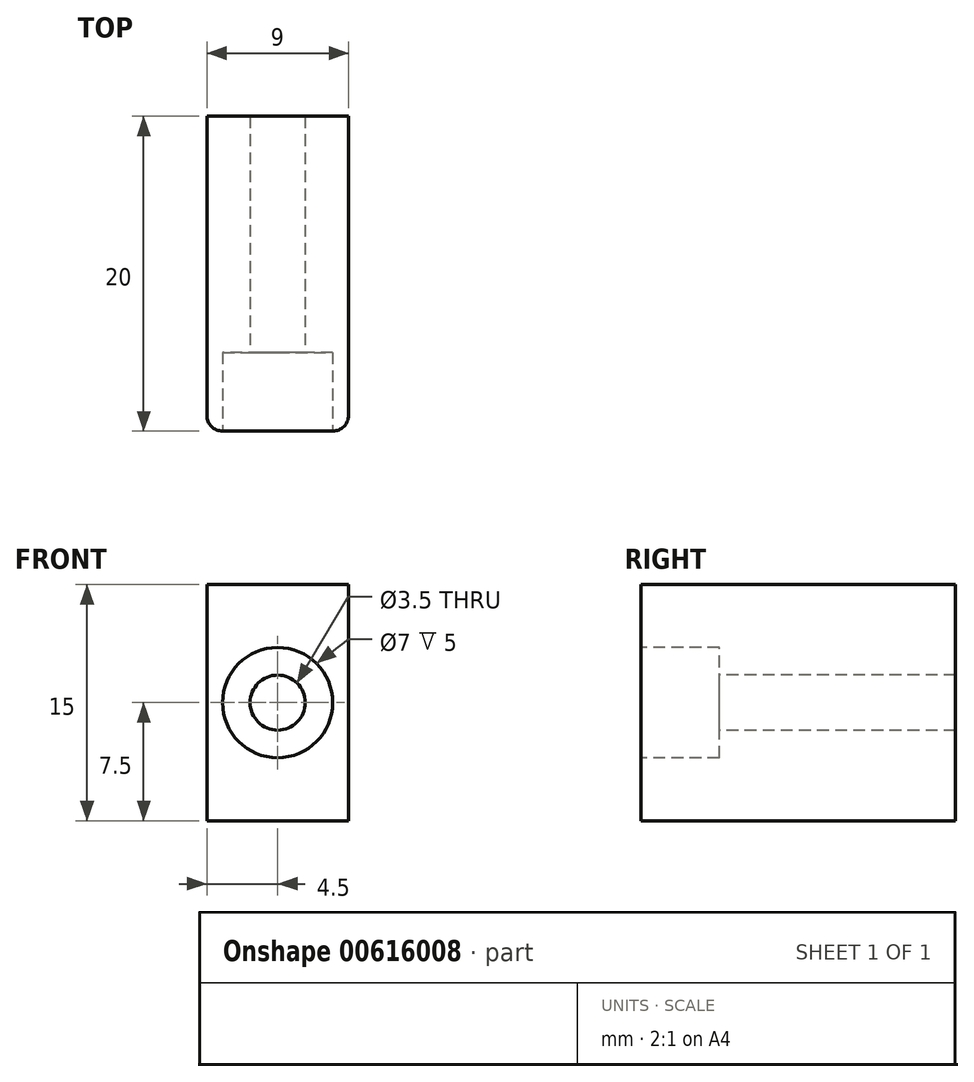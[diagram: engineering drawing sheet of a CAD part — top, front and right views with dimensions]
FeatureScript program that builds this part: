
annotation { "Feature Type Name" : "Feature", "Feature Type Description" : "" }
export const myFeature = defineFeature(function(context is Context, id is Id, definition is map)
    precondition{}
    {
        {
            var Q0;
            Q0=qCreatedBy(makeId("Front.planeOp"),FACE);
            var sketch = newSketch(context, id + "F0", { "sketchPlane" : qUnion([Q0])});
            skLineSegment(sketch, "E0.bottom", {"start": v(-4.5, 7.5) * mm, "end": v(4.5, 7.5) * mm});
            skLineSegment(sketch, "E0.top", {"start": v(-4.5, -7.5) * mm, "end": v(4.5, -7.5) * mm});
            skLineSegment(sketch, "E0.left", {"start": v(-4.5, 7.5) * mm, "end": v(-4.5, -7.5) * mm});
            skLineSegment(sketch, "E0.right", {"start": v(4.5, 7.5) * mm, "end": v(4.5, -7.5) * mm});
            skPoint(sketch, "E0.middle", {"position": v(0, 0) * mm});
            skSolve(sketch);
        }
        {
            var Q0;
            Q0 = qSketchRegion(id + "F0", true);
            extrude(context, id + "F1", {"entities" : qUnion([Q0]), "depth" : 20 * mm, "offsetDistance" : 25 * mm});
        }
        {
            var Q0;
            Q0=makeQuery(id+"F1.opExtrude","CAP_FACE",FACE,{"disambiguationData":[OSD([sQuery(id+"F0.wireOp",EDGE,"E0.bottom"),sQuery(id+"F0.wireOp",EDGE,"E0.top"),sQuery(id+"F0.wireOp",EDGE,"E0.left"),sQuery(id+"F0.wireOp",EDGE,"E0.right")])],"isStart":false});
            var sketch = newSketch(context, id + "F2", { "sketchPlane" : qUnion([Q0])});
            skCircle(sketch, "E1", {"center": v(0, 0) * mm, "radius": 1.75 * mm});
            skPoint(sketch, "E1.centerSnap0", {"position": v(0, 7.5) * mm});
            skSolve(sketch);
        }
        {
            var Q0;
            Q0 = qSketchRegion(id + "F2", true);
            extrude(context, id + "F3", {"entities" : qUnion([Q0]), "operationType" : NewBodyOperationType.REMOVE, "endBound" : BoundingType.THROUGH_ALL, "oppositeDirection" : true, "depth" : 25 * mm, "offsetDistance" : 25 * mm});
        }
        {
            var Q0;
            Q0=makeQuery(id+"F1.opExtrude","CAP_FACE",FACE,{"disambiguationData":[OSD([sQuery(id+"F0.wireOp",EDGE,"E0.bottom"),sQuery(id+"F0.wireOp",EDGE,"E0.top"),sQuery(id+"F0.wireOp",EDGE,"E0.left"),sQuery(id+"F0.wireOp",EDGE,"E0.right")])],"isStart":false});
            var sketch = newSketch(context, id + "F4", { "sketchPlane" : qUnion([Q0])});
            skCircle(sketch, "E2", {"center": v(0, 0) * mm, "radius": 3.5 * mm});
            skSolve(sketch);
        }
        {
            var Q0;
            Q0 = qSketchRegion(id + "F4", true);
            extrude(context, id + "F5", {"entities" : qUnion([Q0]), "operationType" : NewBodyOperationType.REMOVE, "oppositeDirection" : true, "depth" : 5 * mm, "offsetDistance" : 25 * mm});
        }
        {
            var Q0;
            Q0=makeQuery(id+"F1.opExtrude","CAP_EDGE",EDGE,{"disambiguationData":[OSD([sQuery(id+"F0.wireOp",EDGE,"E0.right")])],"isStart":false});
            var Q1;
            Q1=makeQuery(id+"F1.opExtrude","CAP_EDGE",EDGE,{"disambiguationData":[OSD([sQuery(id+"F0.wireOp",EDGE,"E0.left")])],"isStart":false});
            fillet(context, id + "F6", {"entities" : qUnion([Q0, Q1]), "radius" : 1 * mm, "tangentPropagation" : true, "allowEdgeOverflow" : false});
        }
    });
